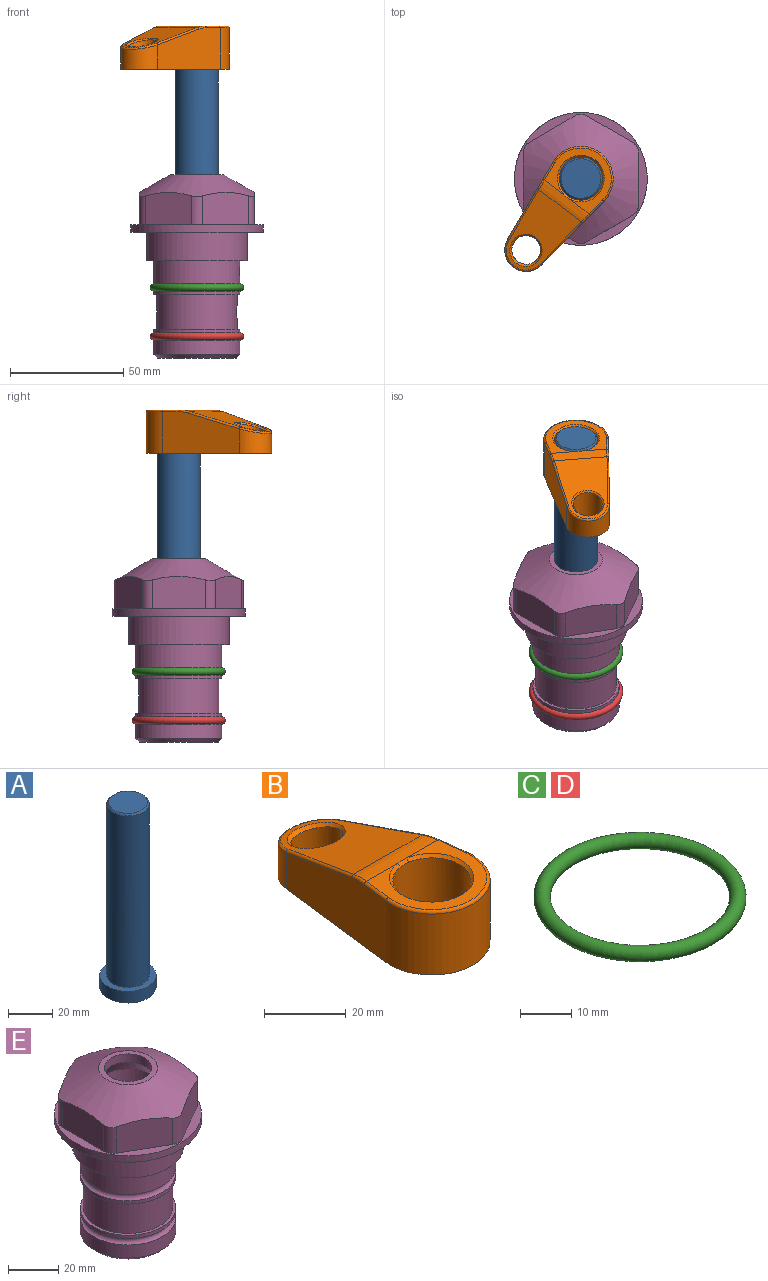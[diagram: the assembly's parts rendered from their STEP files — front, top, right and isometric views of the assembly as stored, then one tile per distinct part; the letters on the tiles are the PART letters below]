
ASSEMBLY  parts=5 mates=4
PART A: 6 faces, bbox 25.4x25.4x101.6 mm
  f0: plane 17.46x17.46mm, normal (0,0,1), area 239.5mm2, adj f5
  f1: plane 25.4x25.4mm, normal (0,0,-1), area 506.7mm2, adj f2
  f2: cylinder r=12.7mm len=25.4mm, axis (0,0,1), area 506.7mm2, adj f1,f3
  f3: plane 25.4x25.4mm, normal (0,0,1), area 221.7mm2, adj f2,f4
  f4: cylinder r=9.53mm len=94.46mm, axis (0,0,1), area 5653mm2, adj f3,f5
  f5: cone r=8.73mm half-angle=45deg, axis (0,0,-1), area 64.4mm2, adj f0,f4
PART B: 31 faces, bbox 31.7x65.5x19.8 mm
  f0: plane 39.12x18.26mm, normal (0.99,0.12,0), area 612.2mm2, adj f1,f4,f7,f11,f13,f15
  f1: cylinder r=9.53mm len=18.91mm, axis (0,0,-1), area 296.1mm2, adj f0,f2,f7,f17
  f2: plane 39.12x18.26mm, normal (-0.99,0.12,0), area 612.2mm2, adj f1,f4,f7,f12,f14,f16
  f3: cylinder r=6.35mm len=12.7mm, axis (0,0,-1), area 362.4mm2, adj f7,f18
  f4: cylinder r=14.29mm len=28.58mm, axis (0,0,-1), area 882.2mm2, adj f0,f2,f7,f10
  f5: cylinder r=9.53mm len=19.05mm, axis (0,0,-1), area 1092.6mm2, adj f7,f19,f20
  f6: plane 26.99x23.69mm, normal (0,0,1), area 216.2mm2, adj f9,f10,f11,f12,f19
  f7: plane 63.5x28.58mm, normal (0,0,-1), area 661.8mm2, adj f0,f1,f2,f3,f4,f5,f22,f23
  f8: plane 33.52x23.6mm, normal (0,0.26,0.97), area 486mm2, adj f9,f15,f16,f17,f18
  f9: cylinder r=19.05mm len=24.72mm, axis (1,0,0), area 120.4mm2, adj f6,f8,f13,f14,f20
  f10: torus R=13.49mm, axis (0,0,1), area 59mm2, adj f4,f6,f11,f12
  f11: cylinder r=0.79mm len=8.67mm, axis (0.12,-0.99,0), area 10.8mm2, adj f0,f6,f10,f13
  f12: cylinder r=0.79mm len=8.67mm, axis (0.12,0.99,0), area 10.8mm2, adj f2,f6,f10,f14
  f13: bspline ~4.95x1.42mm, area 6.1mm2, adj f0,f9,f11,f15
  f14: bspline ~4.95x1.42mm, area 6.1mm2, adj f2,f9,f12,f16
  f15: cylinder r=0.79mm len=25.95mm, axis (0.12,-0.96,0.26), area 32.9mm2, adj f0,f8,f13,f17
  f16: cylinder r=0.79mm len=25.95mm, axis (0.12,0.96,-0.26), area 32.9mm2, adj f2,f8,f14,f17
  f17: bspline ~18.91x8.38mm, area 30mm2, adj f1,f8,f15,f16
  f18: bspline ~14.29x14.29mm, area 48.3mm2, adj f3,f8
  f19: cone r=9.53mm half-angle=45deg, axis (0,0,1), area 66.5mm2, adj f5,f6,f20
  f20: bspline ~3.22x0.96mm, area 3.5mm2, adj f5,f9,f19
  f21: plane 2.75x2.72mm, normal (0,0,-1), area 2.9mm2, adj f23,f25,f28
  f22: plane 23.05x15.88mm, normal (-0.99,-0.12,0), area 323.6mm2, adj f7,f25,f26,f27,f28,f29
  f23: plane 23.05x15.88mm, normal (0.99,-0.12,0), area 323.6mm2, adj f7,f21,f25,f27,f28,f30
  f24: cylinder r=9.53mm len=10.69mm, axis (0,0,-1), area 114.7mm2, adj f7,f27,f29,f30
  f25: cylinder r=12.7mm len=20.59mm, axis (0,0,-1), area 381.1mm2, adj f7,f21,f22,f23,f26,f28
  f26: plane 2.75x2.72mm, normal (0,0,-1), area 2.9mm2, adj f22,f25,f28
  f27: plane 19.72x18.37mm, normal (0,-0.26,-0.97), area 291.8mm2, adj f22,f23,f24,f28,f29,f30
  f28: cylinder r=15.88mm len=19.92mm, axis (1,0,0), area 54.8mm2, adj f21,f22,f23,f25,f26,f27
  f29: cylinder r=1.59mm len=11mm, axis (0,0,-1), area 34.7mm2, adj f7,f22,f24,f27
  f30: cylinder r=1.59mm len=11mm, axis (0,0,-1), area 34.7mm2, adj f7,f23,f24,f27
PART C: 1 faces, bbox 44.7x44.7x3.2 mm
  f0: torus R=19.05mm, axis (0,0,1), area 1193.9mm2
PART D: same geometry as C
PART E: 36 faces, bbox 58.7x58.7x81 mm
  f0: cylinder r=17.78mm len=35.56mm, axis (0,0,1), area 1670.8mm2, adj f23,f24,f31
  f1: cylinder r=19.05mm len=38.1mm, axis (0,0,1), area 1191.9mm2, adj f26,f27,f30
  f2: plane 58.66x58.66mm, normal (0,0,-1), area 1150.6mm2, adj f3,f28
  f3: cylinder r=29.33mm len=58.66mm, axis (0,0,-1), area 585.1mm2, adj f2,f4
  f4: plane 58.66x58.66mm, normal (0,0,1), area 475.9mm2, adj f3,f5,f6,f7,f8,f9,f10,f11
  f5: plane 20.32x14.34mm, normal (-0.5,0.87,0), area 324.4mm2, adj f4,f15,f16,f17
  f6: plane 20.32x14.34mm, normal (0.5,0.87,0), area 324.4mm2, adj f4,f14,f15,f17
  f7: plane 23.48x14.34mm, normal (1,0,0), area 324.4mm2, adj f4,f13,f14,f17
  f8: plane 20.32x14.34mm, normal (0.5,-0.87,0), area 324.4mm2, adj f4,f12,f13,f17
  f9: plane 20.32x14.34mm, normal (-0.5,-0.87,0), area 324.4mm2, adj f4,f11,f12,f17
  f10: plane 23.48x14.34mm, normal (-1,0,0), area 324.4mm2, adj f4,f11,f16,f17
  f11: cylinder r=5.08mm len=12.85mm, axis (0,0,-1), area 67.2mm2, adj f4,f9,f10,f17
  f12: cylinder r=5.08mm len=12.85mm, axis (0,0,-1), area 67.2mm2, adj f4,f8,f9,f17
  f13: cylinder r=5.08mm len=12.85mm, axis (0,0,-1), area 67.2mm2, adj f4,f7,f8,f17
  f14: cylinder r=5.08mm len=12.85mm, axis (0,0,-1), area 67.2mm2, adj f4,f6,f7,f17
  f15: cylinder r=5.08mm len=12.85mm, axis (0,0,-1), area 67.2mm2, adj f4,f5,f6,f17
  f16: cylinder r=5.08mm len=12.85mm, axis (0,0,-1), area 67.2mm2, adj f4,f5,f10,f17
  f17: cone r=11.73mm half-angle=60deg, axis (0,0,-1), area 2071.8mm2, adj f5,f6,f7,f8,f9,f10,f11,f12
  f18: plane 23.46x23.46mm, normal (0,0,1), area 147.4mm2, adj f17,f35
  f19: plane 34.93x34.93mm, normal (0,0,-1), area 958mm2, adj f29
  f20: cylinder r=19.05mm len=38.1mm, axis (0,0,1), area 760.1mm2, adj f21,f29
  f21: torus R=19.05mm, axis (0,0,1), area 565.3mm2, adj f20,f22
  f22: cylinder r=19.05mm len=38.1mm, axis (0,0,1), area 190mm2, adj f21,f23
  f23: plane 38.1x38.1mm, normal (0,0,1), area 146.9mm2, adj f0,f22
  f24: plane 38.1x38.1mm, normal (0,0,-1), area 146.9mm2, adj f0,f25
  f25: cylinder r=19.05mm len=38.1mm, axis (0,0,1), area 190mm2, adj f24,f26
  f26: torus R=19.05mm, axis (0,0,1), area 565.3mm2, adj f1,f25
  f27: plane 44.45x44.45mm, normal (0,0,-1), area 411.7mm2, adj f1,f28
  f28: cylinder r=22.23mm len=44.45mm, axis (0,0,1), area 1773.5mm2, adj f2,f27
  f29: cone r=19.05mm half-angle=45deg, axis (0,0,1), area 257.5mm2, adj f19,f20
  f30: cylinder r=3.17mm len=6.75mm, axis (-1,0,0), area 128mm2, adj f1,f33
  f31: cylinder r=3.17mm len=6.35mm, axis (-1,0,0), area 102.5mm2, adj f0,f33
  f32: plane 25.4x25.4mm, normal (0,0,1), area 506.7mm2, adj f33
  f33: cylinder r=12.7mm len=66.42mm, axis (0,0,-1), area 5236.2mm2, adj f30,f31,f32,f34
  f34: cone r=9.53mm half-angle=30deg, axis (0,0,-1), area 443.4mm2, adj f33,f35
  f35: cylinder r=9.53mm len=19.05mm, axis (0,0,-1), area 240.9mm2, adj f18,f34
PLACE A rot(axis=(0,0,1),142.6deg) t=(0,0,27.55)mm
PLACE B rot(axis=(0,0,1),142.6deg) t=(0,0,27.55)mm
PLACE C at identity
PLACE D t=(0,0,-21.59)mm
PLACE E at identity fixed
MATE fastened D.f0 <-> E.f0  axis (0,0,1) through (0,0,-46.1)mm
MATE fastened C.f0 <-> E.f0  axis (0,0,1) through (0,0,-24.51)mm
MATE fastened A.f2 <-> B.f4  axis (0,0,1) through (0,0,91.05)mm
MATE cylindrical A.f2 <-> E.f0  axis (0,0,-1) through (0,0,-10.55)mm
